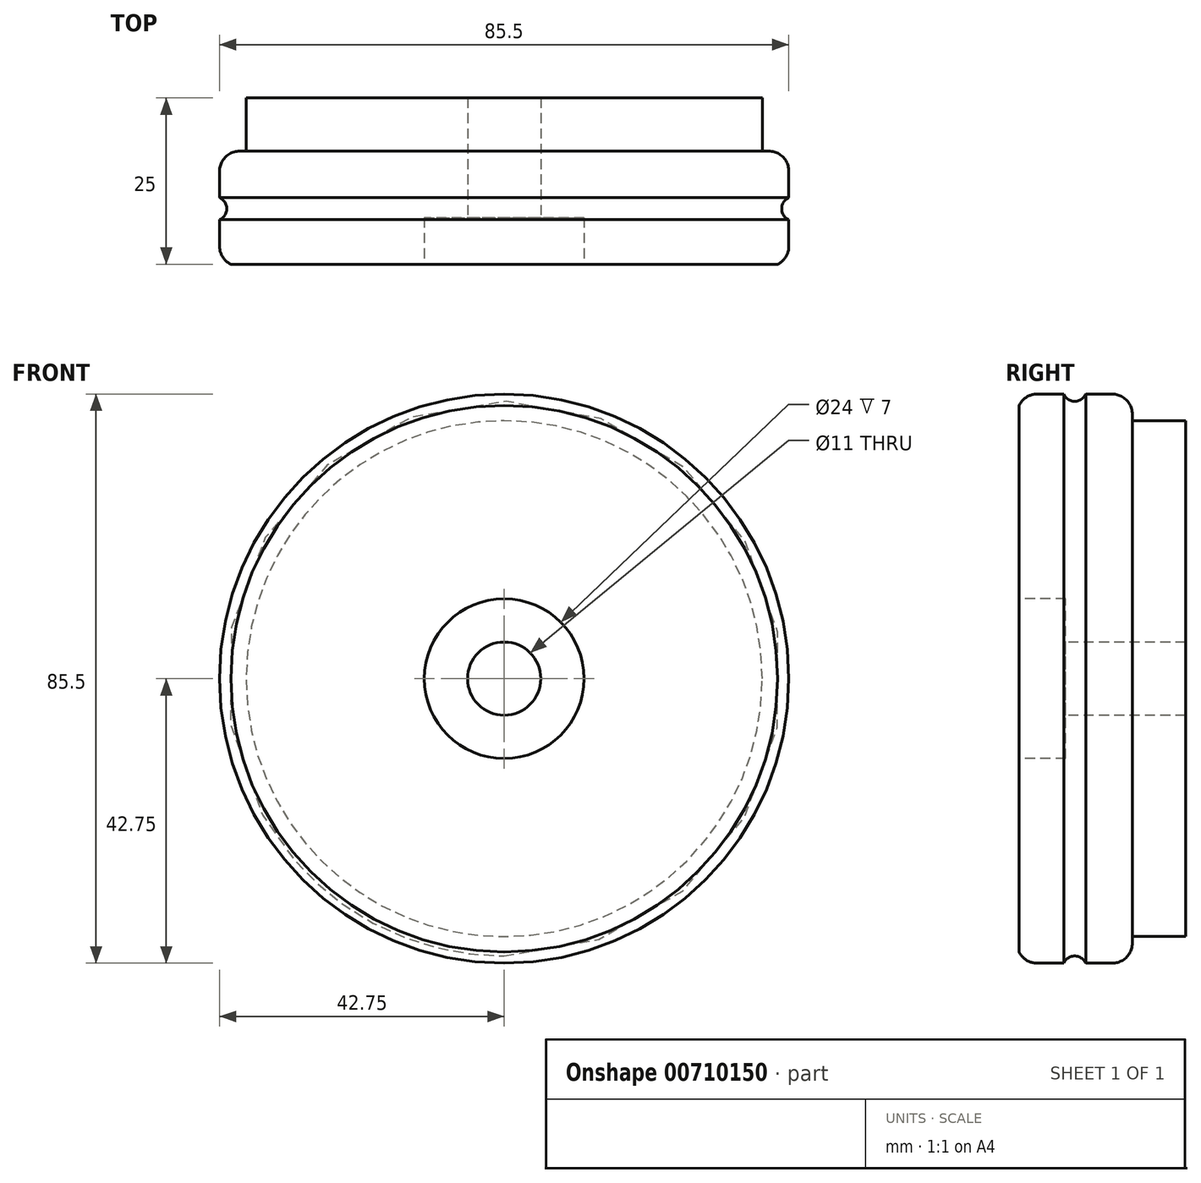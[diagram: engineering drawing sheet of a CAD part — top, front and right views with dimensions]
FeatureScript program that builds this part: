
annotation { "Feature Type Name" : "Feature", "Feature Type Description" : "" }
export const myFeature = defineFeature(function(context is Context, id is Id, definition is map)
    precondition{}
    {
        {
            var Q0;
            Q0=qCreatedBy(makeId("Right.planeOp"),FACE);
            var sketch = newSketch(context, id + "F0", { "sketchPlane" : qUnion([Q0])});
            skLineSegment(sketch, "E0", {"start": v(0, 38.75) * mm, "end": v(0, 39.75) * mm});
            skLineSegment(sketch, "E1", {"start": v(8, 38.75) * mm, "end": v(0, 38.75) * mm});
            skLineSegment(sketch, "E2", {"start": v(8, 38.75) * mm, "end": v(8, 5.5) * mm});
            skPoint(sketch, "E3.visualSharp", {"position": v(-17, 42.75) * mm});
            skArc(sketch, "E3.filletArc", {"start": v(-14.3, 42.75) * mm, "mid": v(-15.9, 42.3) * mm, "end": v(-17, 41.06) * mm});
            skLineSegment(sketch, "E4", {"start": v(-17, 12) * mm, "end": v(-10, 12) * mm});
            skLineSegment(sketch, "E5", {"start": v(-10, 12) * mm, "end": v(-10, 5.5) * mm});
            skLineSegment(sketch, "E6", {"start": v(-10, 5.5) * mm, "end": v(8, 5.5) * mm});
            skLineSegment(sketch, "E7", {"start": v(-17, 41.06) * mm, "end": v(-17, 12) * mm});
            skPoint(sketch, "E8.visualSharp", {"position": v(0, 42.75) * mm});
            skArc(sketch, "E8.filletArc", {"start": v(0, 39.75) * mm, "mid": v(-0.88, 41.87) * mm, "end": v(-3, 42.75) * mm});
            skLineSegment(sketch, "E9", {"start": v(-53.4, 0) * mm, "end": v(53.67, 0) * mm, "construction": true});
            skArc(sketch, "E10", {"start": v(-10.3, 42.75) * mm, "mid": v(-8.65, 41.67) * mm, "end": v(-7, 42.75) * mm});
            skLineSegment(sketch, "E11", {"start": v(-14.3, 42.75) * mm, "end": v(-10.3, 42.75) * mm});
            skLineSegment(sketch, "E12", {"start": v(-3, 42.75) * mm, "end": v(-7, 42.75) * mm});
            skSolve(sketch);
        }
        {
            var Q0;
            Q0=makeQuery(id+"F0.imprint","IMPRINT",FACE,{"disambiguationData":[TD([[makeQuery(id+"F0.imprint","IMPRINT",EDGE,{"derivedFrom":sQuery(id+"F0.wireOp",EDGE,"E0")}),1.0]])]});
            var Q1;
            Q1=sQuery(id+"F0.wireOp",EDGE,"E9");
            revolve(context, id + "F1", {"surfaceOperationType" : NewSurfaceOperationType.NEW, "entities" : qUnion([Q0]), "axis" : qUnion([Q1]), "revolveType" : RevolveType.FULL});
        }
    });
